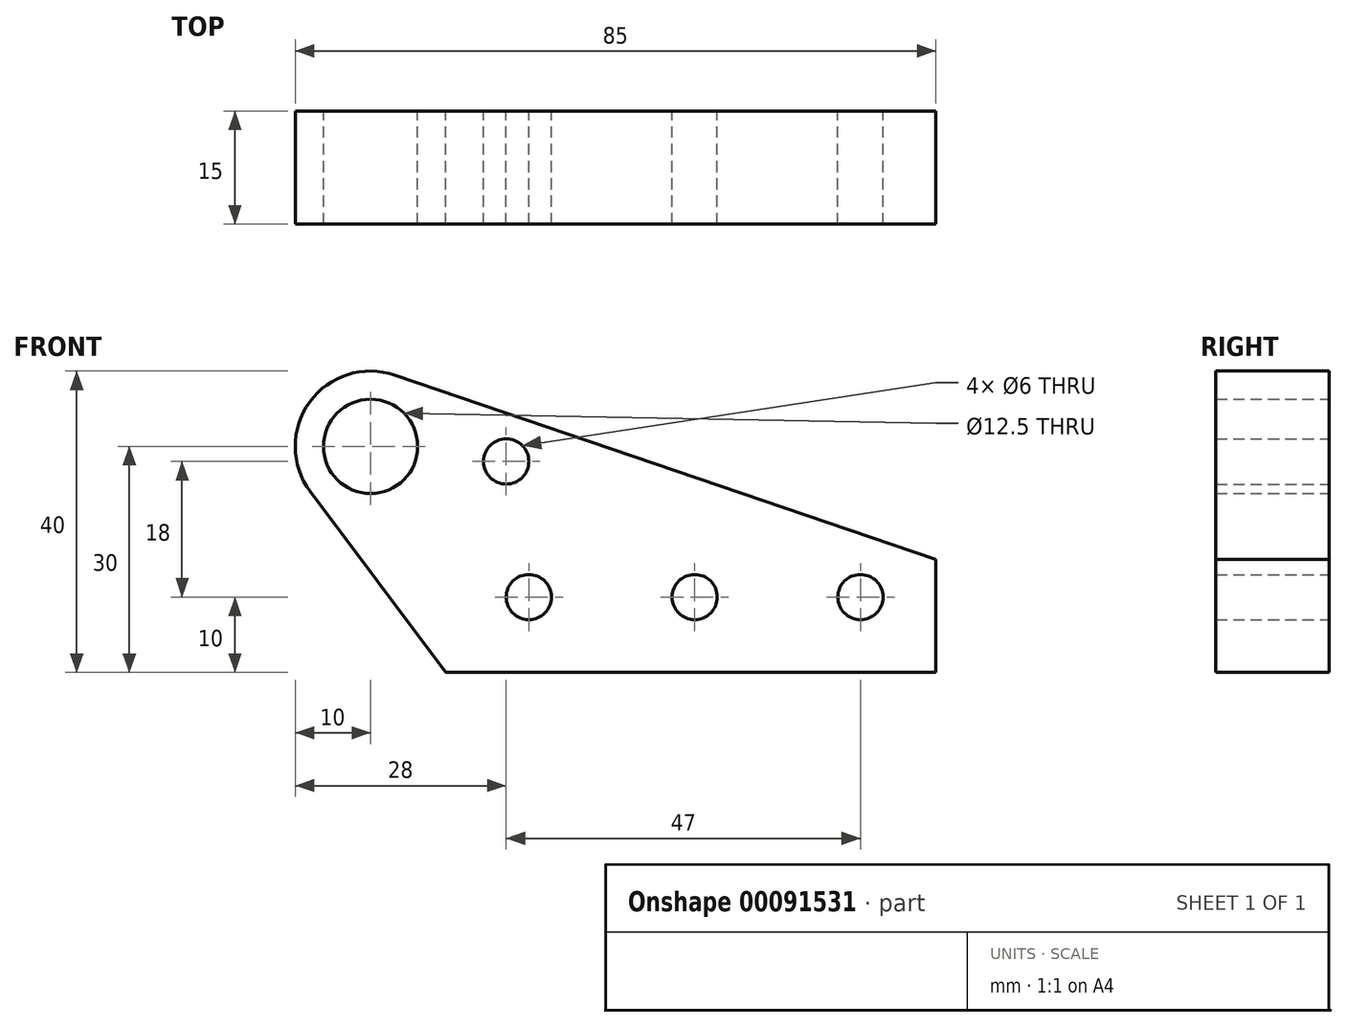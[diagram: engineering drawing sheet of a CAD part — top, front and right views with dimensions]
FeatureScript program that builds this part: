
annotation { "Feature Type Name" : "Feature", "Feature Type Description" : "" }
export const myFeature = defineFeature(function(context is Context, id is Id, definition is map)
    precondition{}
    {
        {
            var Q0;
            Q0=qCreatedBy(makeId("Front.planeOp"),FACE);
            var sketch = newSketch(context, id + "F0", { "sketchPlane" : qUnion([Q0])});
            skLineSegment(sketch, "E0", {"start": v(0, 0) * mm, "end": v(-65, 0) * mm});
            skLineSegment(sketch, "E1", {"start": v(-65, 0) * mm, "end": v(-83, 24) * mm});
            skLineSegment(sketch, "E2", {"start": v(-71.77, 39.47) * mm, "end": v(0, 15) * mm});
            skLineSegment(sketch, "E3", {"start": v(0, 15) * mm, "end": v(0, 0) * mm});
            skPoint(sketch, "E4.visualSharp", {"position": v(-102.44, 49.92) * mm});
            skArc(sketch, "E4.filletArc", {"start": v(-71.77, 39.47) * mm, "mid": v(-83.1, 35.87) * mm, "end": v(-83, 24) * mm});
            skCircle(sketch, "E5", {"center": v(-75, 30) * mm, "radius": 6.25 * mm});
            skCircle(sketch, "E6", {"center": v(-10, 10) * mm, "radius": 3 * mm});
            skCircle(sketch, "E7.1.0.0", {"center": v(-32, 10) * mm, "radius": 3 * mm});
            skCircle(sketch, "E7.2.0.0", {"center": v(-54, 10) * mm, "radius": 3 * mm});
            skLineSegment(sketch, "E7.direction1", {"start": v(-10, 10) * mm, "end": v(-32, 10) * mm, "construction": true});
            skCircle(sketch, "E8", {"center": v(-57, 28) * mm, "radius": 3 * mm});
            skSolve(sketch);
        }
        {
            var Q0;
            Q0=makeQuery(id+"F0.imprint","IMPRINT",FACE,{"disambiguationData":[TD([[makeQuery(id+"F0.imprint","IMPRINT",EDGE,{"derivedFrom":sQuery(id+"F0.wireOp",EDGE,"E0")}),-1.0]])]});
            extrude(context, id + "F1", {"entities" : qUnion([Q0]), "depth" : 15 * mm});
        }
    });
